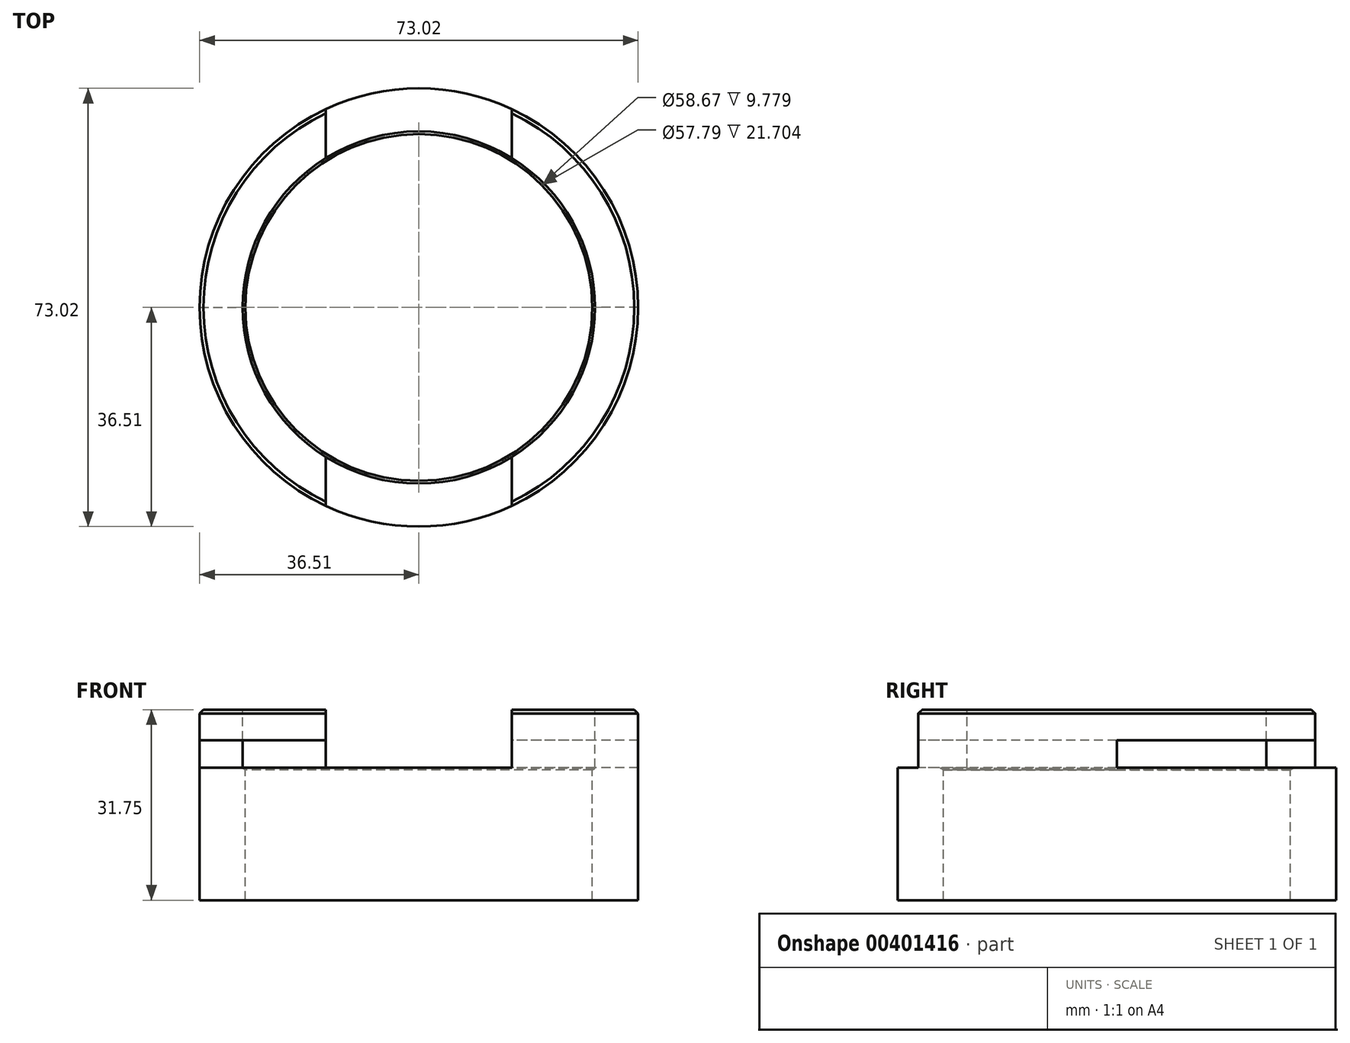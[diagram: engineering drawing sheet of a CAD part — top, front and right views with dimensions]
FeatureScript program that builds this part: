
annotation { "Feature Type Name" : "Feature", "Feature Type Description" : "" }
export const myFeature = defineFeature(function(context is Context, id is Id, definition is map)
    precondition{}
    {
        {
            var Q0;
            Q0=qCreatedBy(makeId("Top.planeOp"),FACE);
            var sketch = newSketch(context, id + "F0", { "sketchPlane" : qUnion([Q0])});
            skCircle(sketch, "E0", {"center": v(0, 0) * mm, "radius": 36.51 * mm});
            skSolve(sketch);
        }
        {
            var Q0;
            Q0=makeQuery(id+"F0.imprint","IMPRINT",FACE,{"disambiguationData":[TD([[makeQuery(id+"F0.imprint","IMPRINT",EDGE,{"derivedFrom":sQuery(id+"F0.wireOp",EDGE,"E0")}),1.0]])]});
            extrude(context, id + "F1", {"entities" : qUnion([Q0]), "oppositeDirection" : true, "depth" : 31.75 * mm});
        }
        {
            var Q0;
            Q0=sQuery(id+"F0.wireOp",VERTEX,"E0.center");
            var Q1;
            Q1=makeQuery(id+"F1.opExtrude","SWEPT_BODY",BODY,{"disambiguationData":[OSD([sQuery(id+"F0.wireOp",EDGE,"E0")])]});
            hole(context, id + "F2", {"style" : HoleStyle.SIMPLE, "endStyle" : HoleEndStyle.THROUGH, "holeDiameter" : 57.78 * mm, "isTappedThrough" : true, "tappedDepth" : 12.7 * mm, "tapClearance" : 3, "locations" : qUnion([Q0]), "scope" : qUnion([Q1])});
        }
        {
            var Q0;
            Q0=sQuery(id+"F0.wireOp",VERTEX,"E0.center");
            var Q1;
            Q1=makeQuery(id+"F1.opExtrude","SWEPT_BODY",BODY,{"disambiguationData":[OSD([sQuery(id+"F0.wireOp",EDGE,"E0")])]});
            hole(context, id + "F3", {"style" : HoleStyle.SIMPLE, "endStyle" : HoleEndStyle.BLIND, "holeDiameter" : 58.67 * mm, "holeDepth" : 9.78 * mm, "isTappedThrough" : true, "tappedDepth" : 12.7 * mm, "tapClearance" : 3, "startFromSketch" : true, "locations" : qUnion([Q0]), "scope" : qUnion([Q1])});
        }
        {
            var Q0;
            Q0=makeQuery(id+"F1.opExtrude","CAP_EDGE",EDGE,{"disambiguationData":[OSD([sQuery(id+"F0.wireOp",EDGE,"E0")])],"isStart":true});
            chamfer(context, id + "F4", {"entities" : qUnion([Q0]), "width" : 0.64 * mm, "tangentPropagation" : true});
        }
        {
            var Q0;
            Q0=qCreatedBy(makeId("Top.planeOp"),FACE);
            cPlane(context, id + "F5", {"entities" : qUnion([Q0]), "cplaneType" : CPlaneType.OFFSET, "offset" : 7.37 * mm, "oppositeDirection" : true, "width" : 152.4 * mm, "height" : 152.4 * mm});
        }
        {
            var Q0;
            Q0=qCreatedBy(id+"F5.planeOp",FACE);
            var sketch = newSketch(context, id + "F6", { "sketchPlane" : qUnion([Q0])});
            skCircle(sketch, "E1.0", {"center": v(0, 0) * mm, "radius": 36.51 * mm});
            skSolve(sketch);
        }
        {
            var Q0;
            Q0=qCreatedBy(makeId("Front.planeOp"),FACE);
            var sketch = newSketch(context, id + "F7", { "sketchPlane" : qUnion([Q0])});
            skLineSegment(sketch, "E2.bottom", {"start": v(-42.98, -5.08) * mm, "end": v(-23.68, -5.08) * mm});
            skLineSegment(sketch, "E2.top", {"start": v(-42.98, -9.65) * mm, "end": v(-23.68, -9.65) * mm});
            skLineSegment(sketch, "E2.left", {"start": v(-42.98, -5.08) * mm, "end": v(-42.98, -9.65) * mm});
            skLineSegment(sketch, "E2.right", {"start": v(-23.68, -5.08) * mm, "end": v(-23.68, -9.65) * mm});
            skLineSegment(sketch, "E3", {"start": v(0, 2.45) * mm, "end": v(0, -38) * mm});
            skLineSegment(sketch, "E4.MirrorCS", {"start": v(42.98, -5.08) * mm, "end": v(23.68, -5.08) * mm});
            skLineSegment(sketch, "E5.MirrorCS", {"start": v(42.98, -5.08) * mm, "end": v(42.98, -9.65) * mm});
            skLineSegment(sketch, "E6.MirrorCS", {"start": v(42.98, -9.65) * mm, "end": v(23.68, -9.65) * mm});
            skLineSegment(sketch, "E7.MirrorCS", {"start": v(23.68, -5.08) * mm, "end": v(23.68, -9.65) * mm});
            skSolve(sketch);
        }
        {
            var Q0;
            Q0 = qSketchRegion(id + "F7", true);
            var Q1;
            Q1=sQuery(id+"F7.wireOp",EDGE,"E3");
            revolve(context, id + "F8", {"operationType" : NewBodyOperationType.REMOVE, "entities" : qUnion([Q0]), "axis" : qUnion([Q1]), "revolveType" : RevolveType.ONE_DIRECTION, "oppositeDirection" : true, "angle" : 90 * degree});
        }
        {
            var Q0;
            Q0=qCreatedBy(makeId("Front.planeOp"),FACE);
            var sketch = newSketch(context, id + "F9", { "sketchPlane" : qUnion([Q0])});
            skLineSegment(sketch, "E8.bottom", {"start": v(-15.5, 0) * mm, "end": v(15.5, 0) * mm});
            skLineSegment(sketch, "E8.top", {"start": v(-15.5, -9.65) * mm, "end": v(15.5, -9.65) * mm});
            skLineSegment(sketch, "E8.left", {"start": v(-15.5, 0) * mm, "end": v(-15.5, -9.65) * mm});
            skLineSegment(sketch, "E8.right", {"start": v(15.5, 0) * mm, "end": v(15.5, -9.65) * mm});
            skSolve(sketch);
        }
        {
            var Q0;
            Q0=makeQuery(id+"F9.imprint","IMPRINT",FACE,{"disambiguationData":[TD([[makeQuery(id+"F9.imprint","IMPRINT",EDGE,{"derivedFrom":sQuery(id+"F9.wireOp",EDGE,"E8.bottom")}),-1.0]])]});
            extrude(context, id + "F10", {"entities" : qUnion([Q0]), "operationType" : NewBodyOperationType.REMOVE, "endBound" : BoundingType.SYMMETRIC, "oppositeDirection" : true, "depth" : 101.6 * mm});
        }
    });
